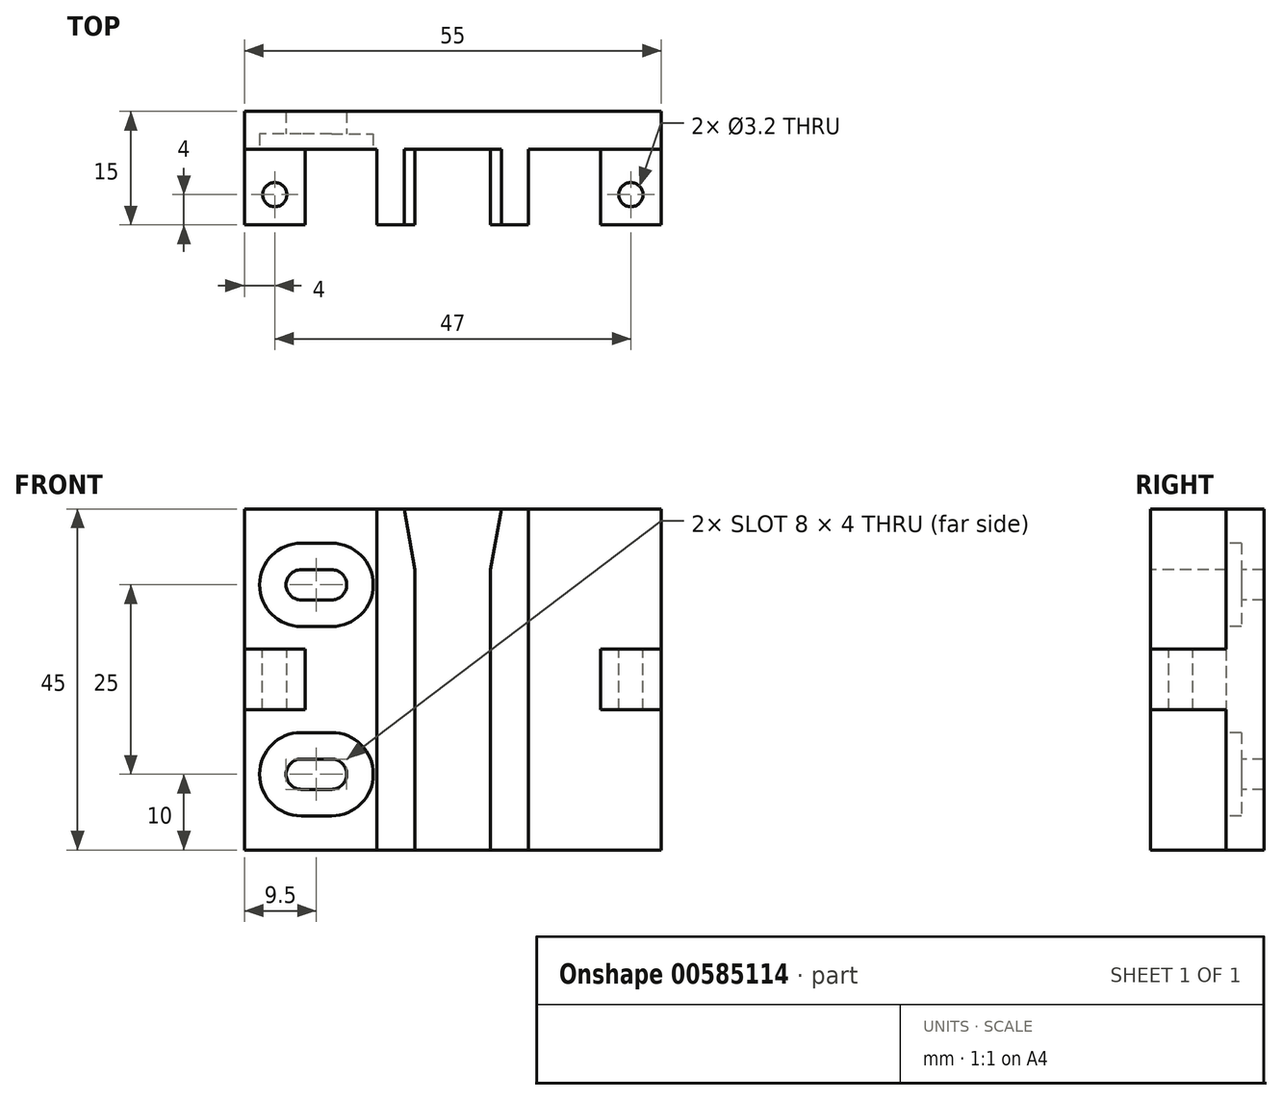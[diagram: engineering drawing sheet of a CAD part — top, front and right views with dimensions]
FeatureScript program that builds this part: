
annotation { "Feature Type Name" : "Feature", "Feature Type Description" : "" }
export const myFeature = defineFeature(function(context is Context, id is Id, definition is map)
    precondition{}
    {
        {
            var Q0;
            Q0=qCreatedBy(makeId("Top.planeOp"),FACE);
            var sketch = newSketch(context, id + "F0", { "sketchPlane" : qUnion([Q0])});
            skLineSegment(sketch, "E0", {"start": v(-5, 0) * mm, "end": v(5, 0) * mm});
            skLineSegment(sketch, "E1", {"start": v(5, 0) * mm, "end": v(5, -10) * mm});
            skLineSegment(sketch, "E2", {"start": v(5, -10) * mm, "end": v(10, -10) * mm});
            skLineSegment(sketch, "E3", {"start": v(27.5, 0) * mm, "end": v(27.5, 5) * mm});
            skLineSegment(sketch, "E4", {"start": v(27.5, 5) * mm, "end": v(-27.5, 5) * mm});
            skLineSegment(sketch, "E5", {"start": v(-27.5, 5) * mm, "end": v(-27.5, 0) * mm});
            skLineSegment(sketch, "E6", {"start": v(-10, -10) * mm, "end": v(-5, -10) * mm});
            skLineSegment(sketch, "E7", {"start": v(-5, -10) * mm, "end": v(-5, 0) * mm});
            skPoint(sketch, "E8", {"position": v(0, 0) * mm});
            skLineSegment(sketch, "E9", {"start": v(-10, -10) * mm, "end": v(-10, 0) * mm});
            skLineSegment(sketch, "E10", {"start": v(-10, 0) * mm, "end": v(-27.5, 0) * mm});
            skLineSegment(sketch, "E11", {"start": v(10, -10) * mm, "end": v(10, 0) * mm});
            skLineSegment(sketch, "E12", {"start": v(10, 0) * mm, "end": v(27.5, 0) * mm});
            skSolve(sketch);
        }
        {
            var Q0;
            Q0 = qSketchRegion(id + "F0", true);
            extrude(context, id + "F1", {"entities" : qUnion([Q0]), "depth" : 45 * mm, "offsetDistance" : 25 * mm});
        }
        {
            var Q0;
            Q0=makeQuery(id+"F1.opExtrude","SWEPT_FACE",FACE,{"disambiguationData":[OSD([sQuery(id+"F0.wireOp",EDGE,"E10")])]});
            var sketch = newSketch(context, id + "F2", { "sketchPlane" : qUnion([Q0])});
            skLineSegment(sketch, "E13.bottom", {"start": v(-20, 37) * mm, "end": v(-16, 37) * mm});
            skLineSegment(sketch, "E13.top", {"start": v(-20, 33) * mm, "end": v(-16, 33) * mm});
            skLineSegment(sketch, "E13.left", {"start": v(-20, 37) * mm, "end": v(-20, 33) * mm, "construction": true});
            skLineSegment(sketch, "E13.right", {"start": v(-16, 37) * mm, "end": v(-16, 33) * mm, "construction": true});
            skArc(sketch, "E14", {"start": v(-20, 37) * mm, "mid": v(-22, 35) * mm, "end": v(-20, 33) * mm});
            skArc(sketch, "E15", {"start": v(-16, 33) * mm, "mid": v(-14, 35) * mm, "end": v(-16, 37) * mm});
            skArc(sketch, "E16.1.0.0", {"start": v(-16, 8) * mm, "mid": v(-14, 10) * mm, "end": v(-16, 12) * mm});
            skArc(sketch, "E16.1.0.1", {"start": v(-20, 12) * mm, "mid": v(-22, 10) * mm, "end": v(-20, 8) * mm});
            skLineSegment(sketch, "E16.1.0.2", {"start": v(-16, 12) * mm, "end": v(-16, 8) * mm, "construction": true});
            skLineSegment(sketch, "E16.1.0.3", {"start": v(-20, 12) * mm, "end": v(-20, 8) * mm, "construction": true});
            skLineSegment(sketch, "E16.1.0.4", {"start": v(-20, 8) * mm, "end": v(-16, 8) * mm});
            skLineSegment(sketch, "E16.1.0.5", {"start": v(-20, 12) * mm, "end": v(-16, 12) * mm});
            skLineSegment(sketch, "E16.direction1", {"start": v(-20, 33) * mm, "end": v(-20, 8) * mm, "construction": true});
            skPoint(sketch, "E17", {"position": v(-18, 37) * mm});
            skSolve(sketch);
        }
        {
            var Q0;
            Q0 = qSketchRegion(id + "F2", true);
            extrude(context, id + "F3", {"entities" : qUnion([Q0]), "operationType" : NewBodyOperationType.REMOVE, "endBound" : BoundingType.UP_TO_NEXT, "oppositeDirection" : true, "depth" : 25 * mm, "offsetDistance" : 25 * mm});
        }
        {
            var Q0;
            Q0=makeQuery(id+"F1.opExtrude","SWEPT_FACE",FACE,{"disambiguationData":[OSD([sQuery(id+"F0.wireOp",EDGE,"E10")])]});
            var sketch = newSketch(context, id + "F4", { "sketchPlane" : qUnion([Q0])});
            skArc(sketch, "E18.0", {"start": v(-20, 40.5) * mm, "mid": v(-25.5, 35) * mm, "end": v(-20, 29.5) * mm});
            skLineSegment(sketch, "E18.1", {"start": v(-20, 40.5) * mm, "end": v(-16, 40.5) * mm});
            skArc(sketch, "E18.2", {"start": v(-16, 29.5) * mm, "mid": v(-10.5, 35) * mm, "end": v(-16, 40.5) * mm});
            skLineSegment(sketch, "E18.3", {"start": v(-20, 29.5) * mm, "end": v(-16, 29.5) * mm});
            skArc(sketch, "E19", {"start": v(-20, 15.5) * mm, "mid": v(-25.5, 10) * mm, "end": v(-20, 4.5) * mm});
            skArc(sketch, "E20", {"start": v(-16, 15.5) * mm, "mid": v(-10.5, 10) * mm, "end": v(-16, 4.5) * mm});
            skLineSegment(sketch, "E21", {"start": v(-20, 15.5) * mm, "end": v(-16, 15.5) * mm});
            skLineSegment(sketch, "E22", {"start": v(-20, 4.5) * mm, "end": v(-16, 4.5) * mm});
            skSolve(sketch);
        }
        {
            var Q0;
            Q0 = qSketchRegion(id + "F4", true);
            extrude(context, id + "F5", {"entities" : qUnion([Q0]), "operationType" : NewBodyOperationType.REMOVE, "oppositeDirection" : true, "depth" : 2 * mm, "offsetDistance" : 25 * mm});
        }
        {
            var Q0;
            Q0=makeQuery(id+"F1.opExtrude","CAP_EDGE",EDGE,{"disambiguationData":[OSD([sQuery(id+"F0.wireOp",EDGE,"E7")])],"isStart":false});
            var Q1;
            Q1=makeQuery(id+"F1.opExtrude","CAP_EDGE",EDGE,{"disambiguationData":[OSD([sQuery(id+"F0.wireOp",EDGE,"E1")])],"isStart":false});
            chamfer(context, id + "F6", {"entities" : qUnion([Q0, Q1]), "chamferType" : ChamferType.OFFSET_ANGLE, "width" : 8 * mm, "oppositeDirection" : true, "angle" : 10 * degree, "tangentPropagation" : true});
        }
        {
            var Q0;
            Q0=makeQuery(id+"F1.opExtrude","SWEPT_FACE",FACE,{"disambiguationData":[OSD([sQuery(id+"F0.wireOp",EDGE,"E10")])]});
            var sketch = newSketch(context, id + "F7", { "sketchPlane" : qUnion([Q0])});
            skLineSegment(sketch, "E23.bottom", {"start": v(-27.5, 26.5) * mm, "end": v(-19.5, 26.5) * mm});
            skLineSegment(sketch, "E23.top", {"start": v(-27.5, 18.5) * mm, "end": v(-19.5, 18.5) * mm});
            skLineSegment(sketch, "E23.left", {"start": v(-27.5, 26.5) * mm, "end": v(-27.5, 18.5) * mm});
            skLineSegment(sketch, "E23.right", {"start": v(-19.5, 26.5) * mm, "end": v(-19.5, 18.5) * mm});
            skLineSegment(sketch, "E24.bottom", {"start": v(27.5, 26.5) * mm, "end": v(19.5, 26.5) * mm});
            skLineSegment(sketch, "E24.top", {"start": v(27.5, 18.5) * mm, "end": v(19.5, 18.5) * mm});
            skLineSegment(sketch, "E24.left", {"start": v(27.5, 26.5) * mm, "end": v(27.5, 18.5) * mm});
            skLineSegment(sketch, "E24.right", {"start": v(19.5, 26.5) * mm, "end": v(19.5, 18.5) * mm});
            skLineSegment(sketch, "E25", {"start": v(-23.5, 26.5) * mm, "end": v(-23.5, 45) * mm, "construction": true});
            skLineSegment(sketch, "E26", {"start": v(-23.5, 18.5) * mm, "end": v(-23.5, 0) * mm, "construction": true});
            skSolve(sketch);
        }
        {
            var Q0;
            Q0 = qSketchRegion(id + "F7", true);
            extrude(context, id + "F8", {"entities" : qUnion([Q0]), "operationType" : NewBodyOperationType.ADD, "depth" : 10 * mm, "offsetDistance" : 25 * mm});
        }
        {
            var Q0;
            Q0=makeQuery(id+"F8.opExtrude","SWEPT_FACE",FACE,{"disambiguationData":[OSD([sQuery(id+"F7.wireOp",EDGE,"E23.bottom")])]});
            var sketch = newSketch(context, id + "F9", { "sketchPlane" : qUnion([Q0])});
            skCircle(sketch, "E27", {"center": v(-23.5, -6) * mm, "radius": 1.6 * mm});
            skCircle(sketch, "E28", {"center": v(23.5, -6) * mm, "radius": 1.6 * mm});
            skLineSegment(sketch, "E29", {"start": v(-23.5, -6) * mm, "end": v(-23.5, -10) * mm, "construction": true});
            skLineSegment(sketch, "E30", {"start": v(23.5, -6) * mm, "end": v(23.5, -10) * mm, "construction": true});
            skLineSegment(sketch, "E31", {"start": v(-19.5, -6) * mm, "end": v(-23.5, -6) * mm, "construction": true});
            skSolve(sketch);
        }
        {
            var Q0;
            Q0 = qSketchRegion(id + "F9", true);
            extrude(context, id + "F10", {"entities" : qUnion([Q0]), "operationType" : NewBodyOperationType.REMOVE, "endBound" : BoundingType.UP_TO_NEXT, "oppositeDirection" : true, "depth" : 25 * mm, "offsetDistance" : 25 * mm});
        }
    });
